# Revit family: NLRS_27_GM_LIB_LA_MR
name_source: partatom
category: Generic Models
units: mm (PartAtom-declared; Revit-internal decimal feet)

## family parameters
Can host rebar = No
Cut with Voids When Loaded = Yes
Part Type = Normal
Room Calculation Point = No
Round Connector Dimension = Use Diameter
Shared = No

## types (9) — shared parameters
Assembly Code = 27.13
Description = LA Luifel
IfcExportAs = IfcFlowsegment
Manufacturer = Meilof Riks bv
Model = LA
Type Image = <None>
URL = https://www.meilofriks.nl
zero-valued in all types: Default Elevation

## per-type parameters (varying)
| type | 02_Trim | Breedte_Luifel | Hoogte_AK | Hoogte_VK | NLRS_C_Materiaal | set_Hoogte_AK |
| LA Trim 400B | Yes | 400 mm  [stored 1.31234 ft] | 125 mm | 60 mm  [stored 0.19685 ft] | RAL 9010 | 125 mm |
| LA Vlak 400A | No | 400 mm  [stored 1.31234 ft] | 90 mm  [stored 0.295276 ft] | 30 mm  [stored 0.0984252 ft] | RAL 9010 | 90 mm  [stored 0.295276 ft] |
| LA Trim 450B | Yes | 450 mm  [stored 1.47638 ft] | 125 mm | 60 mm  [stored 0.19685 ft] | RAL 9010 | 125 mm |
| LA Trim 500B | Yes | 500 mm  [stored 1.64042 ft] | 125 mm | 60 mm  [stored 0.19685 ft] | RAL 9010 | 125 mm |
| LA Vlak 450A | No | 450 mm  [stored 1.47638 ft] | 90 mm  [stored 0.295276 ft] | 30 mm  [stored 0.0984252 ft] | RAL 9010 | 90 mm  [stored 0.295276 ft] |
| LA Vlak 500A | No | 500 mm  [stored 1.64042 ft] | 90 mm  [stored 0.295276 ft] | 30 mm  [stored 0.0984252 ft] | RAL 9010 | 90 mm  [stored 0.295276 ft] |
| LA Vlak 450B | No | 450 mm  [stored 1.47638 ft] | 115 mm  [stored 0.377297 ft] | 45 mm  [stored 0.147638 ft] | RAL 7036 | 115 mm  [stored 0.377297 ft] |
| LA Vlak 400B | No | 400 mm  [stored 1.31234 ft] | 125 mm | 60 mm  [stored 0.19685 ft] | RAL 7036 | 125 mm |
| LA Vlak 500B | No | 500 mm  [stored 1.64042 ft] | 125 mm | 60 mm  [stored 0.19685 ft] | RAL 7036 | 125 mm |

note: [stored X ft] marks values corroborated as IEEE doubles in the binary element streams (Revit-internal decimal feet)

## geometry (parser evidence)
native form markers: Sweep x18
no freeform markers — native parametric forms only
